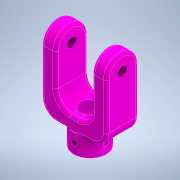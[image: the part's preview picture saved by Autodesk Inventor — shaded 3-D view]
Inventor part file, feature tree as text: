
AUTODESK INVENTOR PART (.ipt)
format: ipt  version: 2022 (Build 260153000, 153)  size: 313,856 bytes
history: native  units: in
note: dims shown in document units (in); Inventor stores cm internally (conversion verified against a paired STEP export)
features: extrude x5, sketch x5, fillet x4, plane x1, other x1, pattern_circular x1
ambient origin geometry x8: Origin, YZ Plane, XZ Plane, XY Plane, X Axis, Y Axis, Z Axis, Center Point
bodies: Solid1 (feature_tree)
feature tree (17):
  extrude  "Extrusion1"  Depth=2.6772in
  fillet  "Fillet1"  Radius=0.5906in
  fillet  "Fillet2"  Radius=0.5906in
  fillet  "Fillet3"  Radius=0.5512in
  extrude  "Extrusion2"  Depth=1.3386in TaperAngle=0.0deg
  extrude  "Extrusion3"  Depth=0.6693in
  fillet  "Fillet4"  Radius=0.5906in
  plane  "Work Plane1"
  extrude  "Extrusion4"  Depth=0.6693in
  other  "Work Axis1"
  pattern_circular  "Circular Pattern1"  Count=2  [1 undecoded]
  extrude  "Extrusion5"  Depth=0.3937in
  sketch  "Sketch1"  dims[d0=3.1496in d1=2.6772in d2=0.5906in d3=0.5906in d4=0.5512in]
  sketch  "Sketch2"  dims[d5=1.4961in d6=1.3386in d7=0.0in]
  sketch  "Sketch3"  dims[d8=0.6693in d9=0.6693in d10=0.5906in]
  sketch  "Sketch4"  dims[d11=1.3386in d12=0.6693in]
  sketch  "Sketch5"  dims[d13=1.3386in d14=0.7874in d15=0.0in d16=0.748in d17=0.0in d18=0.0in d19=0.1181in d20=0.6693in d21=0.2362in d22=0.3937in d23=0.6693in d24=0.0in d25=0.0in d26=1.5748in d27=360.0deg d29=0.3976in d30=0.6496in d31=0.6693in d32=0.0in d33=0.0in]
note: 1 required parameter value undecoded (feature->parameter linkage not recoverable at this tier; creation-order binding heuristic only, values carry confidence <= 0.55)
